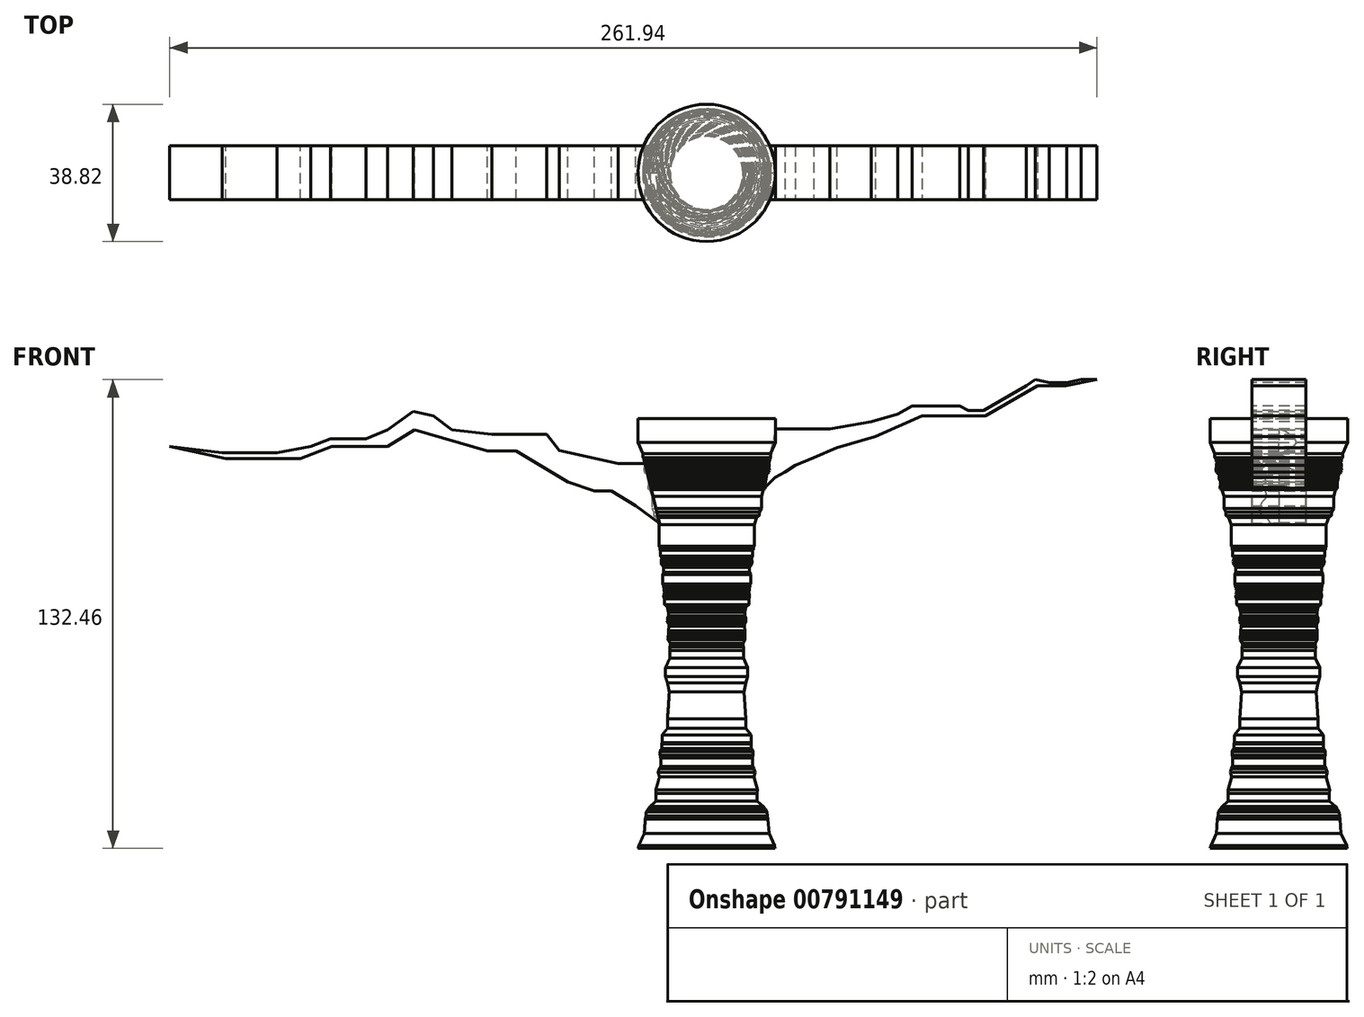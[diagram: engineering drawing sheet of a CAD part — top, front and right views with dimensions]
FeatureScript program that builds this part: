
annotation { "Feature Type Name" : "Feature", "Feature Type Description" : "" }
export const myFeature = defineFeature(function(context is Context, id is Id, definition is map)
    precondition{}
    {
        {
            var Q0;
            Q0=qCreatedBy(makeId("Front.planeOp"),FACE);
            var sketch = newSketch(context, id + "F0", { "sketchPlane" : qUnion([Q0])});
            skLineSegment(sketch, "E0", {"start": v(0, 63.26) * mm, "end": v(0, -58.17) * mm});
            skLineSegment(sketch, "E1", {"start": v(0, -58.17) * mm, "end": v(0, 63.26) * mm});
            skLineSegment(sketch, "E2", {"start": v(0, 63.26) * mm, "end": v(19.4, 63.26) * mm});
            skLineSegment(sketch, "E3", {"start": v(19.4, 63.26) * mm, "end": v(19.4, 58.92) * mm});
            skLineSegment(sketch, "E4", {"start": v(19.4, 58.92) * mm, "end": v(19.4, 56.46) * mm});
            skLineSegment(sketch, "E5", {"start": v(18.07, 53.34) * mm, "end": v(19.4, 56.46) * mm});
            skLineSegment(sketch, "E6", {"start": v(18.07, 53.34) * mm, "end": v(18.07, 52.2) * mm});
            skLineSegment(sketch, "E7", {"start": v(18.07, 52.2) * mm, "end": v(17.66, 51.73) * mm});
            skLineSegment(sketch, "E8", {"start": v(17.7, 51.58) * mm, "end": v(17.66, 51.03) * mm});
            skLineSegment(sketch, "E9", {"start": v(17.66, 51.03) * mm, "end": v(17.4, 50.93) * mm});
            skLineSegment(sketch, "E10", {"start": v(17.4, 50.93) * mm, "end": v(17.66, 50.37) * mm});
            skLineSegment(sketch, "E11", {"start": v(17.66, 50.37) * mm, "end": v(17.66, 49.71) * mm});
            skLineSegment(sketch, "E12", {"start": v(17.6, 49.46) * mm, "end": v(17.7, 49) * mm});
            skLineSegment(sketch, "E13", {"start": v(17.7, 49) * mm, "end": v(17.8, 48.7) * mm});
            skLineSegment(sketch, "E14", {"start": v(17.55, 48.3) * mm, "end": v(17.66, 48) * mm});
            skLineSegment(sketch, "E15", {"start": v(17.66, 48) * mm, "end": v(17.1, 47.74) * mm});
            skLineSegment(sketch, "E16", {"start": v(17.1, 47.74) * mm, "end": v(16.9, 47.28) * mm});
            skLineSegment(sketch, "E17", {"start": v(16.85, 47.03) * mm, "end": v(16.8, 46.32) * mm});
            skLineSegment(sketch, "E18", {"start": v(16.5, 45.46) * mm, "end": v(16.8, 46.32) * mm});
            skLineSegment(sketch, "E19", {"start": v(16.5, 45.46) * mm, "end": v(16.5, 44.76) * mm});
            skLineSegment(sketch, "E20", {"start": v(16.5, 44.76) * mm, "end": v(16.6, 43.95) * mm});
            skLineSegment(sketch, "E21", {"start": v(16.6, 43.95) * mm, "end": v(16.6, 43.5) * mm});
            skLineSegment(sketch, "E22", {"start": v(16.6, 43.5) * mm, "end": v(16.09, 43.24) * mm});
            skLineSegment(sketch, "E23", {"start": v(15.48, 41.22) * mm, "end": v(16.09, 43.24) * mm});
            skLineSegment(sketch, "E24", {"start": v(15.48, 41.22) * mm, "end": v(15.48, 39.57) * mm});
            skLineSegment(sketch, "E25", {"start": v(15.48, 39.57) * mm, "end": v(15.48, 38.88) * mm});
            skLineSegment(sketch, "E26", {"start": v(15.48, 38.88) * mm, "end": v(15.48, 37.81) * mm});
            skLineSegment(sketch, "E27", {"start": v(15.48, 37.81) * mm, "end": v(14.9, 36.8) * mm});
            skLineSegment(sketch, "E28", {"start": v(14.9, 36.8) * mm, "end": v(14.9, 35.87) * mm});
            skLineSegment(sketch, "E29", {"start": v(14.9, 35.87) * mm, "end": v(14.16, 35.33) * mm});
            skLineSegment(sketch, "E30", {"start": v(13.43, 33.32) * mm, "end": v(14.16, 35.33) * mm});
            skLineSegment(sketch, "E31", {"start": v(13.43, 33.32) * mm, "end": v(13.43, 31.26) * mm});
            skLineSegment(sketch, "E32", {"start": v(13.43, 31.26) * mm, "end": v(13.43, 30.28) * mm});
            skLineSegment(sketch, "E33", {"start": v(13.43, 30.28) * mm, "end": v(13.43, 28.54) * mm});
            skLineSegment(sketch, "E34", {"start": v(13.43, 28.54) * mm, "end": v(13.43, 27.46) * mm});
            skLineSegment(sketch, "E35", {"start": v(13.43, 27.46) * mm, "end": v(13.43, 27.12) * mm});
            skLineSegment(sketch, "E36", {"start": v(13.43, 27.12) * mm, "end": v(13.19, 26.8) * mm});
            skLineSegment(sketch, "E37", {"start": v(13.19, 26.8) * mm, "end": v(13.19, 26.51) * mm});
            skLineSegment(sketch, "E38", {"start": v(13.19, 26.51) * mm, "end": v(13.19, 26.15) * mm});
            skLineSegment(sketch, "E39", {"start": v(13.19, 26.15) * mm, "end": v(13, 25.98) * mm});
            skLineSegment(sketch, "E40", {"start": v(13, 25.98) * mm, "end": v(13, 25.79) * mm});
            skLineSegment(sketch, "E41", {"start": v(13, 25.79) * mm, "end": v(13, 25.61) * mm});
            skLineSegment(sketch, "E42", {"start": v(13, 25.61) * mm, "end": v(13, 25.36) * mm});
            skLineSegment(sketch, "E43", {"start": v(13, 25.36) * mm, "end": v(13, 24.59) * mm});
            skLineSegment(sketch, "E44", {"start": v(13, 24.59) * mm, "end": v(13, 24.4) * mm});
            skLineSegment(sketch, "E45", {"start": v(13, 24.4) * mm, "end": v(12.88, 24.14) * mm});
            skLineSegment(sketch, "E46", {"start": v(12.88, 24.14) * mm, "end": v(12.72, 23.98) * mm});
            skLineSegment(sketch, "E47", {"start": v(12.72, 23.98) * mm, "end": v(12.72, 23.85) * mm});
            skLineSegment(sketch, "E48", {"start": v(12.72, 23.85) * mm, "end": v(12.72, 23.67) * mm});
            skLineSegment(sketch, "E49", {"start": v(12.72, 23.67) * mm, "end": v(12.88, 22.88) * mm});
            skLineSegment(sketch, "E50", {"start": v(12.88, 22.88) * mm, "end": v(12.72, 21.98) * mm});
            skLineSegment(sketch, "E51", {"start": v(12.72, 21.98) * mm, "end": v(12.1, 21.21) * mm});
            skLineSegment(sketch, "E52", {"start": v(12.1, 21.21) * mm, "end": v(12.1, 19.86) * mm});
            skLineSegment(sketch, "E53", {"start": v(12.1, 19.86) * mm, "end": v(12.43, 19.2) * mm});
            skLineSegment(sketch, "E54", {"start": v(12.43, 19.2) * mm, "end": v(12.43, 18.57) * mm});
            skLineSegment(sketch, "E55", {"start": v(12.43, 18.57) * mm, "end": v(12.43, 17.7) * mm});
            skLineSegment(sketch, "E56", {"start": v(12.43, 17.7) * mm, "end": v(12.43, 17.07) * mm});
            skLineSegment(sketch, "E57", {"start": v(12.43, 17.07) * mm, "end": v(12.43, 16.69) * mm});
            skLineSegment(sketch, "E58", {"start": v(12.43, 16.69) * mm, "end": v(12.43, 16.45) * mm});
            skLineSegment(sketch, "E59", {"start": v(12.43, 16.45) * mm, "end": v(12.22, 16.18) * mm});
            skLineSegment(sketch, "E60", {"start": v(12.22, 16.18) * mm, "end": v(12.22, 15.9) * mm});
            skLineSegment(sketch, "E61", {"start": v(12.22, 15.9) * mm, "end": v(12.22, 15.67) * mm});
            skLineSegment(sketch, "E62", {"start": v(12.05, 15.3) * mm, "end": v(12.05, 15.02) * mm});
            skLineSegment(sketch, "E63", {"start": v(12.1, 14.7) * mm, "end": v(12.05, 14.57) * mm});
            skLineSegment(sketch, "E64", {"start": v(12.05, 14.57) * mm, "end": v(11.94, 14.48) * mm});
            skLineSegment(sketch, "E65", {"start": v(12.05, 15.02) * mm, "end": v(12.1, 14.7) * mm});
            skLineSegment(sketch, "E66", {"start": v(12.05, 15.3) * mm, "end": v(12.07, 15.37) * mm});
            skLineSegment(sketch, "E67", {"start": v(12.07, 15.37) * mm, "end": v(12.07, 15.4) * mm});
            skLineSegment(sketch, "E68", {"start": v(12.07, 15.4) * mm, "end": v(12.13, 15.46) * mm});
            skLineSegment(sketch, "E69", {"start": v(12.13, 15.46) * mm, "end": v(12.15, 15.51) * mm});
            skLineSegment(sketch, "E70", {"start": v(12.15, 15.51) * mm, "end": v(12.18, 15.59) * mm});
            skLineSegment(sketch, "E71", {"start": v(12.18, 15.59) * mm, "end": v(12.22, 15.67) * mm});
            skLineSegment(sketch, "E72", {"start": v(11.94, 14.48) * mm, "end": v(11.94, 14.3) * mm});
            skLineSegment(sketch, "E73", {"start": v(11.94, 14.3) * mm, "end": v(11.94, 14.18) * mm});
            skLineSegment(sketch, "E74", {"start": v(11.94, 14.18) * mm, "end": v(11.97, 14.05) * mm});
            skLineSegment(sketch, "E75", {"start": v(11.97, 14.05) * mm, "end": v(11.97, 13.96) * mm});
            skLineSegment(sketch, "E76", {"start": v(11.97, 13.96) * mm, "end": v(11.97, 13.8) * mm});
            skLineSegment(sketch, "E77", {"start": v(11.97, 13.8) * mm, "end": v(12.1, 13.61) * mm});
            skLineSegment(sketch, "E78", {"start": v(12.1, 13.61) * mm, "end": v(12.09, 13.46) * mm});
            skLineSegment(sketch, "E79", {"start": v(12.09, 13.46) * mm, "end": v(12.04, 13.35) * mm});
            skLineSegment(sketch, "E80", {"start": v(12.04, 13.35) * mm, "end": v(11.98, 13.26) * mm});
            skLineSegment(sketch, "E81", {"start": v(11.98, 13.26) * mm, "end": v(12.1, 13.18) * mm});
            skLineSegment(sketch, "E82", {"start": v(12.1, 13.18) * mm, "end": v(12.12, 12.84) * mm});
            skLineSegment(sketch, "E83", {"start": v(12.12, 12.84) * mm, "end": v(11.9, 12.3) * mm});
            skLineSegment(sketch, "E84", {"start": v(11.9, 12.3) * mm, "end": v(11.9, 10.72) * mm});
            skLineSegment(sketch, "E85", {"start": v(11.9, 10.72) * mm, "end": v(11.13, 10.07) * mm});
            skLineSegment(sketch, "E86", {"start": v(11.13, 10.07) * mm, "end": v(11, 9.42) * mm});
            skLineSegment(sketch, "E87", {"start": v(11, 9.42) * mm, "end": v(10.8, 8.5) * mm});
            skLineSegment(sketch, "E88", {"start": v(10.8, 7.47) * mm, "end": v(11.07, 6.88) * mm});
            skLineSegment(sketch, "E89", {"start": v(10.8, 8.5) * mm, "end": v(10.8, 7.47) * mm});
            skLineSegment(sketch, "E90", {"start": v(11.07, 6.88) * mm, "end": v(11.07, 6.15) * mm});
            skLineSegment(sketch, "E91", {"start": v(11.07, 6.15) * mm, "end": v(11.13, 5.84) * mm});
            skLineSegment(sketch, "E92", {"start": v(11.13, 5.84) * mm, "end": v(10.56, 4.92) * mm});
            skLineSegment(sketch, "E93", {"start": v(10.56, 4.92) * mm, "end": v(10.65, 4.57) * mm});
            skLineSegment(sketch, "E94", {"start": v(10.65, 4.57) * mm, "end": v(10.78, 3.26) * mm});
            skLineSegment(sketch, "E95", {"start": v(10.78, 3.26) * mm, "end": v(10.78, 2.43) * mm});
            skLineSegment(sketch, "E96", {"start": v(10.78, 2.43) * mm, "end": v(10.87, 1.6) * mm});
            skLineSegment(sketch, "E97", {"start": v(10.87, 1.6) * mm, "end": v(10.87, 0.73) * mm});
            skLineSegment(sketch, "E98", {"start": v(10.87, 0.73) * mm, "end": v(10.3, -0.27) * mm});
            skLineSegment(sketch, "E99", {"start": v(10.3, -0.27) * mm, "end": v(10.3, -1.02) * mm});
            skLineSegment(sketch, "E100", {"start": v(10.3, -1.02) * mm, "end": v(10.43, -1.24) * mm});
            skLineSegment(sketch, "E101", {"start": v(10.43, -1.24) * mm, "end": v(10.39, -2.24) * mm});
            skLineSegment(sketch, "E102", {"start": v(10.39, -2.24) * mm, "end": v(10.39, -4.45) * mm});
            skLineSegment(sketch, "E103", {"start": v(10.39, -4.45) * mm, "end": v(11.62, -7.1) * mm});
            skLineSegment(sketch, "E104", {"start": v(11.62, -7.1) * mm, "end": v(11.62, -9.71) * mm});
            skLineSegment(sketch, "E105", {"start": v(11.62, -9.71) * mm, "end": v(11.05, -11.48) * mm});
            skLineSegment(sketch, "E106", {"start": v(10.54, -14.01) * mm, "end": v(10.8, -17.8) * mm});
            skLineSegment(sketch, "E107", {"start": v(10.8, -17.8) * mm, "end": v(10.54, -14.01) * mm});
            skLineSegment(sketch, "E108", {"start": v(11.05, -11.48) * mm, "end": v(10.54, -14.01) * mm});
            skLineSegment(sketch, "E109", {"start": v(10.8, -17.8) * mm, "end": v(11.05, -21.6) * mm});
            skLineSegment(sketch, "E110", {"start": v(11.05, -21.6) * mm, "end": v(11.05, -24.27) * mm});
            skLineSegment(sketch, "E111", {"start": v(11.05, -24.27) * mm, "end": v(12.6, -26.16) * mm});
            skLineSegment(sketch, "E112", {"start": v(12.6, -26.16) * mm, "end": v(12.6, -28.37) * mm});
            skLineSegment(sketch, "E113", {"start": v(12.6, -28.37) * mm, "end": v(12.65, -28.7) * mm});
            skLineSegment(sketch, "E114", {"start": v(12.65, -28.7) * mm, "end": v(12.65, -29.93) * mm});
            skLineSegment(sketch, "E115", {"start": v(12.65, -29.93) * mm, "end": v(12.99, -30.34) * mm});
            skLineSegment(sketch, "E116", {"start": v(12.99, -30.34) * mm, "end": v(13.12, -30.82) * mm});
            skLineSegment(sketch, "E117", {"start": v(13.12, -30.82) * mm, "end": v(13.12, -31.43) * mm});
            skLineSegment(sketch, "E118", {"start": v(13.12, -31.43) * mm, "end": v(13.12, -31.9) * mm});
            skLineSegment(sketch, "E119", {"start": v(12.99, -32.66) * mm, "end": v(12.99, -33.4) * mm});
            skLineSegment(sketch, "E120", {"start": v(13.12, -31.9) * mm, "end": v(12.99, -32.66) * mm});
            skLineSegment(sketch, "E121", {"start": v(12.99, -33.4) * mm, "end": v(12.99, -35.06) * mm});
            skLineSegment(sketch, "E122", {"start": v(12.99, -35.06) * mm, "end": v(13.42, -35.73) * mm});
            skLineSegment(sketch, "E123", {"start": v(13.42, -35.73) * mm, "end": v(13.7, -36.7) * mm});
            skLineSegment(sketch, "E124", {"start": v(13.7, -36.7) * mm, "end": v(13.32, -38.03) * mm});
            skLineSegment(sketch, "E125", {"start": v(13.32, -38.03) * mm, "end": v(14.37, -41.67) * mm});
            skLineSegment(sketch, "E126", {"start": v(14.37, -41.67) * mm, "end": v(14.28, -42.72) * mm});
            skLineSegment(sketch, "E127", {"start": v(14.28, -42.72) * mm, "end": v(14.28, -44.82) * mm});
            skLineSegment(sketch, "E128", {"start": v(14.28, -44.82) * mm, "end": v(16, -46.35) * mm});
            skLineSegment(sketch, "E129", {"start": v(16, -46.35) * mm, "end": v(16.48, -47.02) * mm});
            skLineSegment(sketch, "E130", {"start": v(16.48, -47.02) * mm, "end": v(17.05, -47.89) * mm});
            skLineSegment(sketch, "E131", {"start": v(17.05, -47.89) * mm, "end": v(17.15, -49.03) * mm});
            skLineSegment(sketch, "E132", {"start": v(17.15, -49.03) * mm, "end": v(17.34, -49.9) * mm});
            skLineSegment(sketch, "E133", {"start": v(17.34, -49.9) * mm, "end": v(17.63, -54) * mm});
            skLineSegment(sketch, "E134", {"start": v(17.63, -54) * mm, "end": v(19.16, -57.36) * mm});
            skLineSegment(sketch, "E135", {"start": v(19.16, -57.36) * mm, "end": v(19.35, -58.22) * mm});
            skLineSegment(sketch, "E136", {"start": v(19.35, -58.22) * mm, "end": v(0, -58.17) * mm});
            skLineSegment(sketch, "E137", {"start": v(17.66, 51.73) * mm, "end": v(17.7, 51.58) * mm});
            skLineSegment(sketch, "E138", {"start": v(17.66, 49.71) * mm, "end": v(17.6, 49.46) * mm});
            skLineSegment(sketch, "E139", {"start": v(17.8, 48.7) * mm, "end": v(17.55, 48.3) * mm});
            skLineSegment(sketch, "E140", {"start": v(16.9, 47.28) * mm, "end": v(16.85, 47.03) * mm});
            skSolve(sketch);
        }
        {
            var Q0;
            Q0 = qSketchRegion(id + "F0", true);
            var Q1;
            Q1=sQuery(id+"F0.wireOp",EDGE,"E1");
            revolve(context, id + "F1", {"surfaceOperationType" : NewSurfaceOperationType.NEW, "entities" : qUnion([Q0]), "axis" : qUnion([Q1]), "revolveType" : RevolveType.FULL});
        }
        {
            var Q0;
            Q0=qCreatedBy(makeId("Front.planeOp"),FACE);
            var sketch = newSketch(context, id + "F2", { "sketchPlane" : qUnion([Q0])});
            skLineSegment(sketch, "E141", {"start": v(16.32, 43.56) * mm, "end": v(19.38, 46.55) * mm});
            skLineSegment(sketch, "E142", {"start": v(19.38, 46.55) * mm, "end": v(22.1, 48.12) * mm});
            skLineSegment(sketch, "E143", {"start": v(22.1, 48.12) * mm, "end": v(25.08, 50.06) * mm});
            skLineSegment(sketch, "E144", {"start": v(25.08, 50.06) * mm, "end": v(30.2, 52.18) * mm});
            skLineSegment(sketch, "E145", {"start": v(30.2, 52.18) * mm, "end": v(36.71, 55) * mm});
            skLineSegment(sketch, "E146", {"start": v(36.71, 55) * mm, "end": v(47.67, 58.21) * mm});
            skLineSegment(sketch, "E147", {"start": v(47.67, 58.21) * mm, "end": v(60.8, 64.02) * mm});
            skLineSegment(sketch, "E148", {"start": v(60.8, 64.02) * mm, "end": v(67.82, 64.02) * mm});
            skLineSegment(sketch, "E149", {"start": v(67.82, 64.02) * mm, "end": v(78.82, 64.02) * mm});
            skLineSegment(sketch, "E150", {"start": v(78.82, 64.02) * mm, "end": v(88.9, 69.82) * mm});
            skLineSegment(sketch, "E151", {"start": v(88.9, 69.82) * mm, "end": v(93.52, 72.48) * mm});
            skLineSegment(sketch, "E152", {"start": v(93.52, 72.48) * mm, "end": v(101.48, 72.48) * mm});
            skLineSegment(sketch, "E153", {"start": v(101.48, 72.48) * mm, "end": v(110.25, 74.24) * mm});
            skLineSegment(sketch, "E154", {"start": v(110.25, 74.24) * mm, "end": v(103, 72.79) * mm});
            skLineSegment(sketch, "E155", {"start": v(110.25, 74.24) * mm, "end": v(105.77, 74.24) * mm});
            skLineSegment(sketch, "E156", {"start": v(105.77, 74.24) * mm, "end": v(101.7, 73.43) * mm});
            skLineSegment(sketch, "E157", {"start": v(101.7, 73.43) * mm, "end": v(96.8, 73.43) * mm});
            skLineSegment(sketch, "E158", {"start": v(96.8, 73.43) * mm, "end": v(92.92, 74.24) * mm});
            skLineSegment(sketch, "E159", {"start": v(92.92, 74.24) * mm, "end": v(90.26, 72.52) * mm});
            skLineSegment(sketch, "E160", {"start": v(90.26, 72.52) * mm, "end": v(78.27, 65.48) * mm});
            skLineSegment(sketch, "E161", {"start": v(78.27, 65.48) * mm, "end": v(73.96, 65.48) * mm});
            skLineSegment(sketch, "E162", {"start": v(73.96, 65.48) * mm, "end": v(71.59, 66.84) * mm});
            skLineSegment(sketch, "E163", {"start": v(61.92, 66.84) * mm, "end": v(58.1, 66.84) * mm});
            skLineSegment(sketch, "E164", {"start": v(58.1, 66.84) * mm, "end": v(54, 64.55) * mm});
            skLineSegment(sketch, "E165", {"start": v(54, 64.55) * mm, "end": v(46.49, 62.36) * mm});
            skLineSegment(sketch, "E166", {"start": v(46.49, 62.36) * mm, "end": v(34.87, 60.31) * mm});
            skLineSegment(sketch, "E167", {"start": v(34.87, 60.31) * mm, "end": v(26, 60.31) * mm});
            skLineSegment(sketch, "E168", {"start": v(26, 60.31) * mm, "end": v(19.43, 60.31) * mm});
            skLineSegment(sketch, "E169", {"start": v(19.43, 60.31) * mm, "end": v(16.32, 43.56) * mm});
            skLineSegment(sketch, "E170", {"start": v(61.92, 66.84) * mm, "end": v(71.59, 66.84) * mm});
            skSolve(sketch);
        }
        {
            var Q0;
            Q0 = qSketchRegion(id + "F2", true);
            extrude(context, id + "F3", {"entities" : qUnion([Q0]), "operationType" : NewBodyOperationType.ADD, "oppositeDirection" : true, "depth" : 7.62 * mm, "offsetDistance" : 25.4 * mm});
        }
        {
            var Q0;
            Q0=makeQuery(id+"F3.opExtrude","CAP_FACE",FACE,{"disambiguationData":[OSD([sQuery(id+"F2.wireOp",EDGE,"E141"),sQuery(id+"F2.wireOp",EDGE,"E142"),sQuery(id+"F2.wireOp",EDGE,"E143"),sQuery(id+"F2.wireOp",EDGE,"E144"),sQuery(id+"F2.wireOp",EDGE,"E145"),sQuery(id+"F2.wireOp",EDGE,"E146"),sQuery(id+"F2.wireOp",EDGE,"E147"),sQuery(id+"F2.wireOp",EDGE,"E148"),sQuery(id+"F2.wireOp",EDGE,"E149"),sQuery(id+"F2.wireOp",EDGE,"E150"),sQuery(id+"F2.wireOp",EDGE,"E151"),sQuery(id+"F2.wireOp",EDGE,"E152"),sQuery(id+"F2.wireOp",EDGE,"E153"),sQuery(id+"F2.wireOp",EDGE,"E154"),sQuery(id+"F2.wireOp",EDGE,"E155"),sQuery(id+"F2.wireOp",EDGE,"E156"),sQuery(id+"F2.wireOp",EDGE,"E157"),sQuery(id+"F2.wireOp",EDGE,"E158"),sQuery(id+"F2.wireOp",EDGE,"E159"),sQuery(id+"F2.wireOp",EDGE,"E160"),sQuery(id+"F2.wireOp",EDGE,"E161"),sQuery(id+"F2.wireOp",EDGE,"E162"),sQuery(id+"F2.wireOp",EDGE,"E163"),sQuery(id+"F2.wireOp",EDGE,"E164"),sQuery(id+"F2.wireOp",EDGE,"E165"),sQuery(id+"F2.wireOp",EDGE,"E166"),sQuery(id+"F2.wireOp",EDGE,"E167"),sQuery(id+"F2.wireOp",EDGE,"E168"),sQuery(id+"F2.wireOp",EDGE,"E169"),sQuery(id+"F2.wireOp",EDGE,"E170")])],"isStart":true});
            extrude(context, id + "F4", {"entities" : qUnion([Q0]), "operationType" : NewBodyOperationType.ADD, "depth" : 7.62 * mm, "offsetDistance" : 25.4 * mm});
        }
        {
            var Q0;
            Q0=qCreatedBy(makeId("Front.planeOp"),FACE);
            var sketch = newSketch(context, id + "F5", { "sketchPlane" : qUnion([Q0])});
            skLineSegment(sketch, "E171", {"start": v(-13.35, 33.6) * mm, "end": v(-19.98, 38.65) * mm});
            skLineSegment(sketch, "E172", {"start": v(-19.98, 38.65) * mm, "end": v(-26.93, 42.76) * mm});
            skLineSegment(sketch, "E173", {"start": v(-26.93, 42.76) * mm, "end": v(-31.67, 42.76) * mm});
            skLineSegment(sketch, "E174", {"start": v(-31.67, 42.76) * mm, "end": v(-39.25, 45.28) * mm});
            skLineSegment(sketch, "E175", {"start": v(-39.25, 45.28) * mm, "end": v(-53.78, 54.13) * mm});
            skLineSegment(sketch, "E176", {"start": v(-53.78, 54.13) * mm, "end": v(-61.99, 54.13) * mm});
            skLineSegment(sketch, "E177", {"start": v(-61.99, 54.13) * mm, "end": v(-82.52, 60.13) * mm});
            skLineSegment(sketch, "E178", {"start": v(-82.52, 60.13) * mm, "end": v(-90.1, 55.4) * mm});
            skLineSegment(sketch, "E179", {"start": v(-90.1, 55.4) * mm, "end": v(-105.9, 55.4) * mm});
            skLineSegment(sketch, "E180", {"start": v(-105.9, 55.4) * mm, "end": v(-114.73, 51.92) * mm});
            skLineSegment(sketch, "E181", {"start": v(-114.73, 51.92) * mm, "end": v(-135.9, 51.92) * mm});
            skLineSegment(sketch, "E182", {"start": v(-135.9, 51.92) * mm, "end": v(-151.69, 55.4) * mm});
            skLineSegment(sketch, "E183", {"start": v(-151.69, 55.4) * mm, "end": v(-136.93, 53.65) * mm});
            skPoint(sketch, "E183.endSnap0", {"position": v(-143.8, 53.65) * mm});
            skLineSegment(sketch, "E184", {"start": v(-136.93, 53.65) * mm, "end": v(-121.43, 53.65) * mm});
            skLineSegment(sketch, "E185", {"start": v(-121.43, 53.65) * mm, "end": v(-111.92, 55.4) * mm});
            skLineSegment(sketch, "E186", {"start": v(-111.92, 55.4) * mm, "end": v(-106.33, 57.59) * mm});
            skLineSegment(sketch, "E187", {"start": v(-106.33, 57.59) * mm, "end": v(-96.3, 57.59) * mm});
            skLineSegment(sketch, "E188", {"start": v(-96.3, 57.59) * mm, "end": v(-90.1, 60.02) * mm});
            skLineSegment(sketch, "E189", {"start": v(-90.1, 60.02) * mm, "end": v(-82.84, 65.26) * mm});
            skLineSegment(sketch, "E190", {"start": v(-82.84, 65.26) * mm, "end": v(-77.23, 64.03) * mm});
            skLineSegment(sketch, "E191", {"start": v(-77.23, 64.03) * mm, "end": v(-71.97, 60.1) * mm});
            skLineSegment(sketch, "E192", {"start": v(-71.97, 60.1) * mm, "end": v(-60.69, 58.74) * mm});
            skLineSegment(sketch, "E193", {"start": v(-60.69, 58.74) * mm, "end": v(-52.53, 58.74) * mm});
            skLineSegment(sketch, "E194", {"start": v(-52.53, 58.74) * mm, "end": v(-45.2, 58.74) * mm});
            skLineSegment(sketch, "E195", {"start": v(-45.2, 58.74) * mm, "end": v(-41.66, 54.26) * mm});
            skLineSegment(sketch, "E196", {"start": v(-41.66, 54.26) * mm, "end": v(-34.36, 52.65) * mm});
            skLineSegment(sketch, "E197", {"start": v(-34.36, 52.65) * mm, "end": v(-24.96, 50.58) * mm});
            skLineSegment(sketch, "E198", {"start": v(-24.96, 50.58) * mm, "end": v(-17.33, 50.58) * mm});
            skLineSegment(sketch, "E199", {"start": v(-17.33, 50.58) * mm, "end": v(-13.35, 33.6) * mm});
            skSolve(sketch);
        }
        {
            var Q0;
            Q0 = qSketchRegion(id + "F5", true);
            extrude(context, id + "F6", {"entities" : qUnion([Q0]), "operationType" : NewBodyOperationType.ADD, "depth" : 7.62 * mm, "offsetDistance" : 25.4 * mm});
        }
        {
            var Q0;
            Q0=makeQuery(id+"F6.opExtrude","CAP_FACE",FACE,{"disambiguationData":[OSD([sQuery(id+"F5.wireOp",EDGE,"E171"),sQuery(id+"F5.wireOp",EDGE,"E172"),sQuery(id+"F5.wireOp",EDGE,"E173"),sQuery(id+"F5.wireOp",EDGE,"E174"),sQuery(id+"F5.wireOp",EDGE,"E175"),sQuery(id+"F5.wireOp",EDGE,"E176"),sQuery(id+"F5.wireOp",EDGE,"E177"),sQuery(id+"F5.wireOp",EDGE,"E178"),sQuery(id+"F5.wireOp",EDGE,"E179"),sQuery(id+"F5.wireOp",EDGE,"E180"),sQuery(id+"F5.wireOp",EDGE,"E181"),sQuery(id+"F5.wireOp",EDGE,"E182"),sQuery(id+"F5.wireOp",EDGE,"E183"),sQuery(id+"F5.wireOp",EDGE,"E184"),sQuery(id+"F5.wireOp",EDGE,"E185"),sQuery(id+"F5.wireOp",EDGE,"E186"),sQuery(id+"F5.wireOp",EDGE,"E187"),sQuery(id+"F5.wireOp",EDGE,"E188"),sQuery(id+"F5.wireOp",EDGE,"E189"),sQuery(id+"F5.wireOp",EDGE,"E190"),sQuery(id+"F5.wireOp",EDGE,"E191"),sQuery(id+"F5.wireOp",EDGE,"E192"),sQuery(id+"F5.wireOp",EDGE,"E193"),sQuery(id+"F5.wireOp",EDGE,"E194"),sQuery(id+"F5.wireOp",EDGE,"E195"),sQuery(id+"F5.wireOp",EDGE,"E196"),sQuery(id+"F5.wireOp",EDGE,"E197"),sQuery(id+"F5.wireOp",EDGE,"E198"),sQuery(id+"F5.wireOp",EDGE,"E199")])],"isStart":true});
            extrude(context, id + "F7", {"entities" : qUnion([Q0]), "operationType" : NewBodyOperationType.ADD, "depth" : 7.62 * mm, "offsetDistance" : 25.4 * mm});
        }
    });
